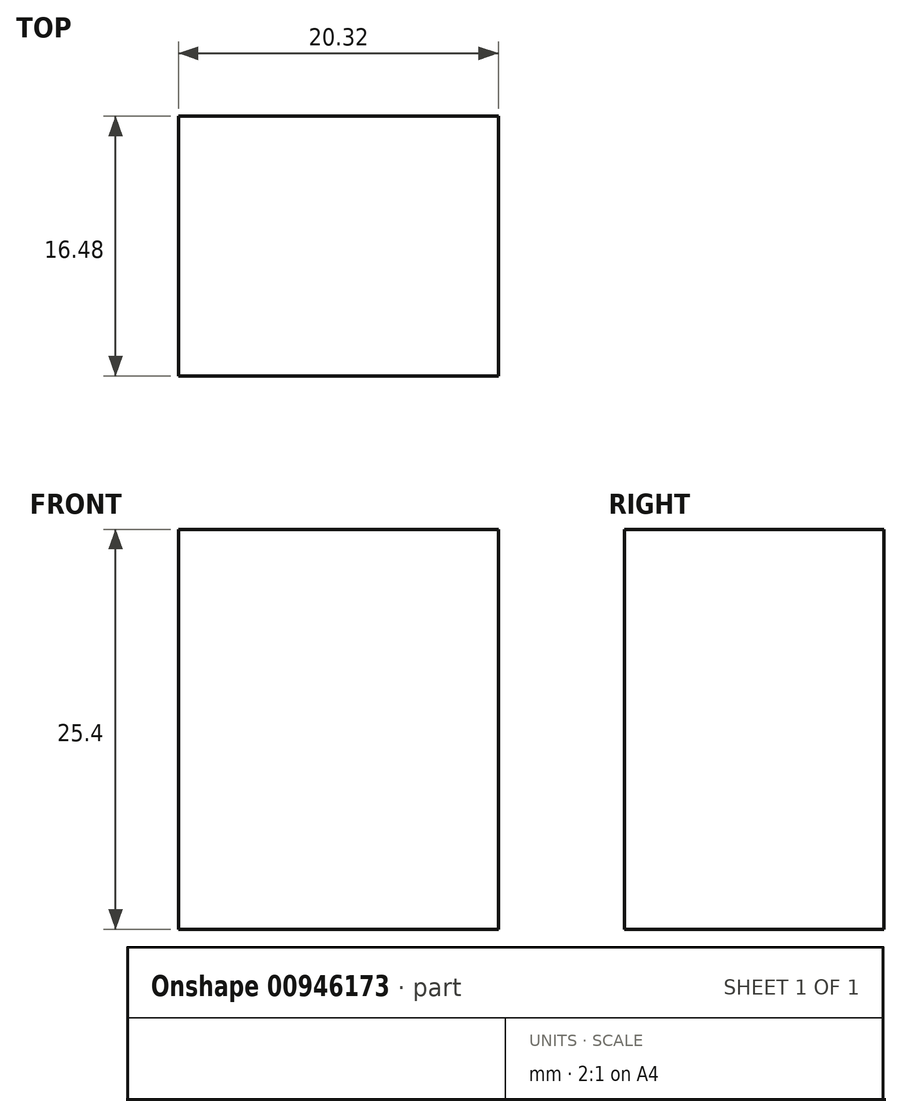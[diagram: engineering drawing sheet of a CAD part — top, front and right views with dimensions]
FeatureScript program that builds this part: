
annotation { "Feature Type Name" : "Feature", "Feature Type Description" : "" }
export const myFeature = defineFeature(function(context is Context, id is Id, definition is map)
    precondition{}
    {
        {
            var Q0;
            Q0=qCreatedBy(makeId("Top.planeOp"),FACE);
            var sketch = newSketch(context, id + "F0", { "sketchPlane" : qUnion([Q0])});
            skLineSegment(sketch, "E0.bottom", {"start": v(0, 0) * mm, "end": v(-20.32, 0) * mm});
            skLineSegment(sketch, "E0.top", {"start": v(0, 16.48) * mm, "end": v(-20.32, 16.48) * mm});
            skLineSegment(sketch, "E0.left", {"start": v(0, 0) * mm, "end": v(0, 16.48) * mm});
            skLineSegment(sketch, "E0.right", {"start": v(-20.32, 0) * mm, "end": v(-20.32, 16.48) * mm});
            skSolve(sketch);
        }
        {
            var Q0;
            Q0=makeQuery(id+"F0.imprint","IMPRINT",FACE,{"disambiguationData":[TD([[makeQuery(id+"F0.imprint","IMPRINT",EDGE,{"derivedFrom":sQuery(id+"F0.wireOp",EDGE,"E0.bottom")}),-1.0]])]});
            extrude(context, id + "F1", {"entities" : qUnion([Q0]), "depth" : 25.4 * mm, "offsetDistance" : 25.4 * mm});
        }
    });
